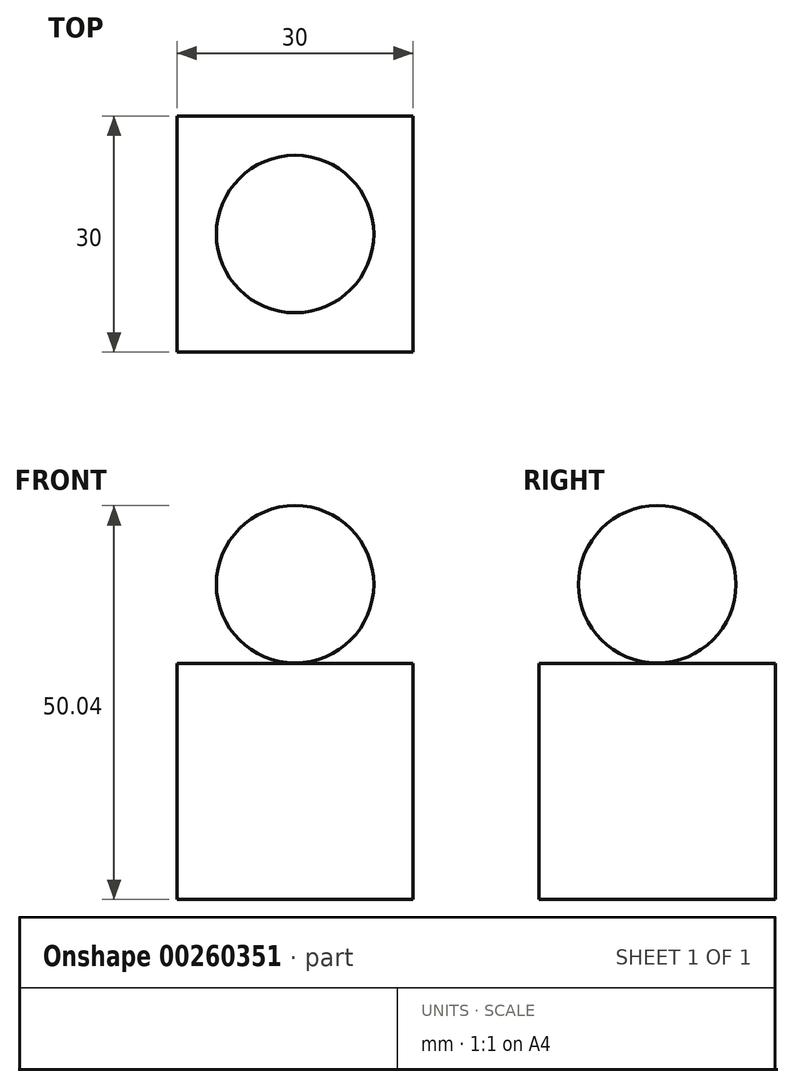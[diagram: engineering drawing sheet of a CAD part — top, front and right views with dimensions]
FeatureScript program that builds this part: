
annotation { "Feature Type Name" : "Feature", "Feature Type Description" : "" }
export const myFeature = defineFeature(function(context is Context, id is Id, definition is map)
    precondition{}
    {
        {
            var Q0;
            Q0=qCreatedBy(makeId("Top.planeOp"),FACE);
            var sketch = newSketch(context, id + "F0", { "sketchPlane" : qUnion([Q0])});
            skLineSegment(sketch, "E0.bottom", {"start": v(15, -15) * mm, "end": v(-15, -15) * mm});
            skLineSegment(sketch, "E0.top", {"start": v(15, 15) * mm, "end": v(-15, 15) * mm});
            skLineSegment(sketch, "E0.left", {"start": v(15, -15) * mm, "end": v(15, 15) * mm});
            skLineSegment(sketch, "E0.right", {"start": v(-15, -15) * mm, "end": v(-15, 15) * mm});
            skPoint(sketch, "E0.middle", {"position": v(0, 0) * mm});
            skSolve(sketch);
        }
        {
            var Q0;
            Q0=makeQuery(id+"F0.imprint","IMPRINT",FACE,{"disambiguationData":[TD([[makeQuery(id+"F0.imprint","IMPRINT",EDGE,{"derivedFrom":sQuery(id+"F0.wireOp",EDGE,"E0.bottom")}),-1.0]])]});
            extrude(context, id + "F1", {"entities" : qUnion([Q0]), "depth" : 30 * mm});
        }
        {
            var Q0;
            Q0=makeQuery(id+"F1.opExtrude","CAP_FACE",FACE,{"disambiguationData":[OSD([sQuery(id+"F0.wireOp",EDGE,"E0.bottom"),sQuery(id+"F0.wireOp",EDGE,"E0.top"),sQuery(id+"F0.wireOp",EDGE,"E0.left"),sQuery(id+"F0.wireOp",EDGE,"E0.right")])],"isStart":false});
            var sketch = newSketch(context, id + "F2", { "sketchPlane" : qUnion([Q0])});
            skCircle(sketch, "E1", {"center": v(0, 0) * mm, "radius": 7.5 * mm});
            skSolve(sketch);
        }
        {
            var Q0;
            Q0=qCreatedBy(makeId("Right.planeOp"),FACE);
            var sketch = newSketch(context, id + "F3", { "sketchPlane" : qUnion([Q0])});
            skArc(sketch, "E2", {"start": v(0, 30.04) * mm, "mid": v(10, 40.04) * mm, "end": v(0, 50.04) * mm});
            skLineSegment(sketch, "E3", {"start": v(0, 50.04) * mm, "end": v(0, 30.04) * mm});
            skSolve(sketch);
        }
        {
            var Q0;
            Q0=makeQuery(id+"F3.imprint","IMPRINT",FACE,{"disambiguationData":[TD([[makeQuery(id+"F3.imprint","IMPRINT",EDGE,{"derivedFrom":sQuery(id+"F3.wireOp",EDGE,"E2")}),1.0]])]});
            var Q1;
            Q1=sQuery(id+"F3.wireOp",EDGE,"E3");
            revolve(context, id + "F4", {"entities" : qUnion([Q0]), "axis" : qUnion([Q1]), "revolveType" : RevolveType.FULL});
        }
    });
